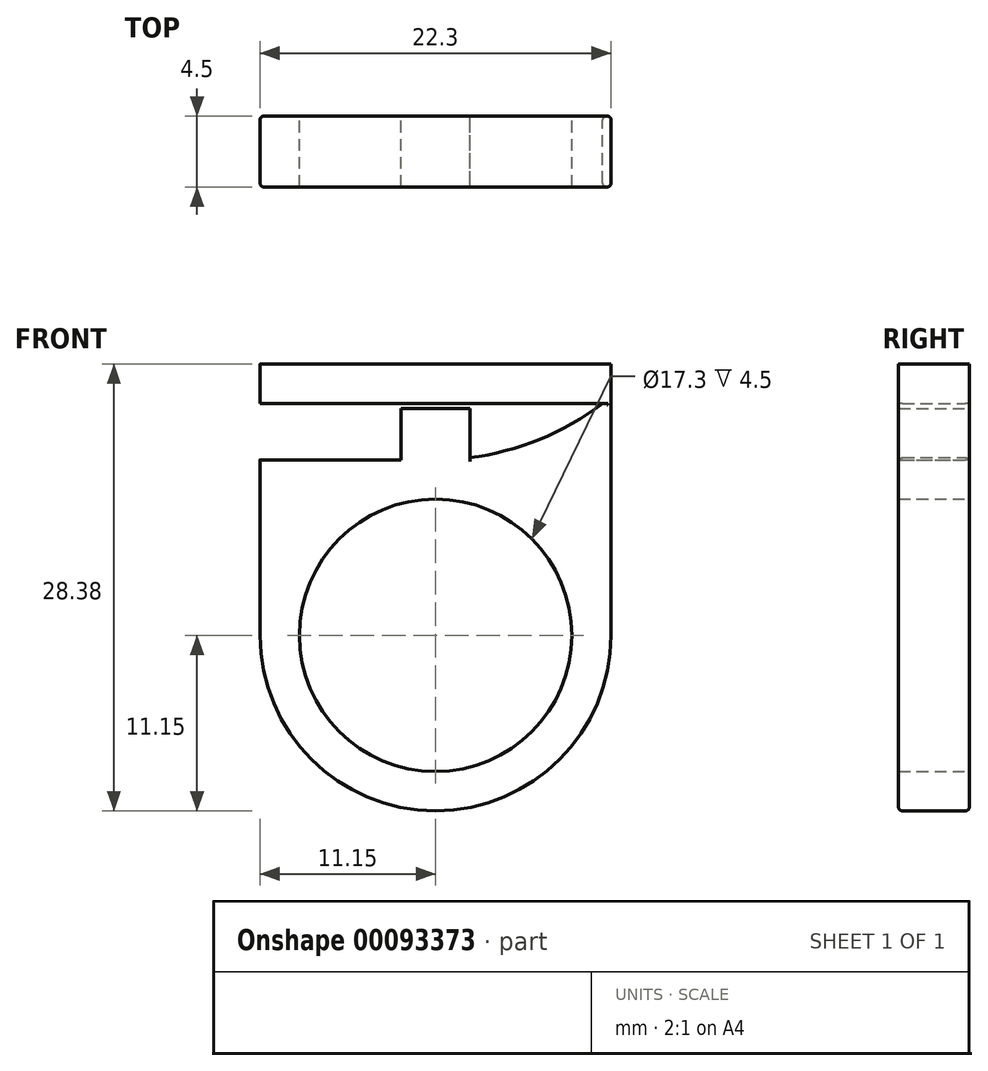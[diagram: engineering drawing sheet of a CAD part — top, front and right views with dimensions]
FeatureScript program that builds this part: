
annotation { "Feature Type Name" : "Feature", "Feature Type Description" : "" }
export const myFeature = defineFeature(function(context is Context, id is Id, definition is map)
    precondition{}
    {
        {
            var Q0;
            Q0=qCreatedBy(makeId("Front.planeOp"),FACE);
            var sketch = newSketch(context, id + "F0", { "sketchPlane" : qUnion([Q0])});
            skCircle(sketch, "E0", {"center": v(0, 0) * mm, "radius": 8.65 * mm});
            skCircle(sketch, "E1.0", {"center": v(0, 0) * mm, "radius": 11.15 * mm});
            skPoint(sketch, "E2", {"position": v(0, 11.15) * mm});
            skPoint(sketch, "E3", {"position": v(11.15, 0) * mm});
            skPoint(sketch, "E4", {"position": v(-11.15, 0) * mm});
            skLineSegment(sketch, "E5", {"start": v(11.15, 0) * mm, "end": v(11.15, 11.15) * mm});
            skLineSegment(sketch, "E6", {"start": v(11.15, 11.15) * mm, "end": v(0, 11.15) * mm});
            skLineSegment(sketch, "E7.MirrorCS", {"start": v(-11.15, 11.15) * mm, "end": v(0, 11.15) * mm});
            skLineSegment(sketch, "E8.MirrorCS", {"start": v(-11.15, 0) * mm, "end": v(-11.15, 11.15) * mm});
            skLineSegment(sketch, "E9", {"start": v(0, 11.15) * mm, "end": v(0, 13.15) * mm, "construction": true});
            skArc(sketch, "E10", {"start": v(0, 11.15) * mm, "mid": v(2, 13.15) * mm, "end": v(0, 15.15) * mm, "construction": true});
            skLineSegment(sketch, "E11", {"start": v(0, 15.15) * mm, "end": v(-11.15, 15.15) * mm});
            skLineSegment(sketch, "E12", {"start": v(-11.15, 15.15) * mm, "end": v(-11.15, 17.23) * mm});
            skLineSegment(sketch, "E13", {"start": v(-11.15, 17.23) * mm, "end": v(11.15, 17.23) * mm});
            skLineSegment(sketch, "E14", {"start": v(11.15, 17.23) * mm, "end": v(11.15, 15.15) * mm});
            skLineSegment(sketch, "E15", {"start": v(11.15, 15.15) * mm, "end": v(0, 15.15) * mm});
            skLineSegment(sketch, "E16", {"start": v(0, 13.15) * mm, "end": v(2, 13.15) * mm});
            skLineSegment(sketch, "E17.MirrorCS", {"start": v(0, 13.15) * mm, "end": v(-2, 13.15) * mm});
            skLineSegment(sketch, "E18", {"start": v(-11.15, 15.15) * mm, "end": v(-11.15, 11.15) * mm, "construction": true});
            skLineSegment(sketch, "E19", {"start": v(-11.15, 13.15) * mm, "end": v(-9.15, 13.15) * mm, "construction": true});
            skArc(sketch, "E20", {"start": v(-9.15, 15.15) * mm, "mid": v(-11.15, 13.15) * mm, "end": v(-9.15, 11.15) * mm, "construction": true});
            skPoint(sketch, "E21", {"position": v(-4, 15.15) * mm});
            skPoint(sketch, "E22", {"position": v(-4, 11.15) * mm});
            skPoint(sketch, "E23", {"position": v(-9.15, 15.15) * mm});
            skPoint(sketch, "E24", {"position": v(-9.15, 11.15) * mm});
            skLineSegment(sketch, "E25", {"start": v(0, 13.15) * mm, "end": v(-4, 13.15) * mm});
            skArc(sketch, "E26", {"start": v(-4, 15.15) * mm, "mid": v(-6, 13.15) * mm, "end": v(-4, 11.15) * mm, "construction": true});
            skArc(sketch, "E27", {"start": v(0, 11.15) * mm, "mid": v(5.92, 12.18) * mm, "end": v(11.15, 15.15) * mm});
            skLineSegment(sketch, "E28", {"start": v(11.15, 15.15) * mm, "end": v(11.15, 11.15) * mm});
            skArc(sketch, "E29.MirrorCS", {"start": v(0, 11.15) * mm, "mid": v(-5.92, 12.18) * mm, "end": v(-11.15, 15.15) * mm});
            skLineSegment(sketch, "E30", {"start": v(-11.15, 15.15) * mm, "end": v(-11.15, 11.15) * mm});
            skLineSegment(sketch, "E31", {"start": v(2.18, 10.75) * mm, "end": v(2.18, 14.42) * mm});
            skLineSegment(sketch, "E32", {"start": v(2.18, 14.42) * mm, "end": v(0, 14.42) * mm});
            skLineSegment(sketch, "E33.MirrorCS", {"start": v(-2.18, 14.42) * mm, "end": v(0, 14.42) * mm});
            skLineSegment(sketch, "E34.MirrorCS", {"start": v(-2.18, 10.75) * mm, "end": v(-2.18, 14.42) * mm});
            skPoint(sketch, "E35.start.orphan", {"position": v(0, 10.75) * mm});
            skPoint(sketch, "E36.MirrorCS.end.orphan", {"position": v(-2.18, 10.75) * mm});
            skLineSegment(sketch, "E37", {"start": v(-11.15, 14.71) * mm, "end": v(11.15, 14.71) * mm});
            skSolve(sketch);
        }
        {
            var Q0;
            Q0=makeQuery(id+"F0.imprint","IMPRINT",FACE,{"disambiguationData":[TD([[makeQuery(id+"F0.imprint","IMPRINT",EDGE,{"derivedFrom":sQuery(id+"F0.wireOp",EDGE,"E0")}),-1.0]])]});
            var Q1;
            {var subQ0=sQuery(id+"F0.wireOp",EDGE,"E7.MirrorCS");Q1=makeQuery(id+"F0.imprint","IMPRINT",FACE,{"disambiguationData":[TD([[makeQuery(id+"F0.imprint","IMPRINT",EDGE,{"derivedFrom":subQ0}),-1.0]])]});}
            var Q2;
            {var subQ0=sQuery(id+"F0.wireOp",EDGE,"E5");Q2=makeQuery(id+"F0.imprint","IMPRINT",FACE,{"disambiguationData":[TD([[makeQuery(id+"F0.imprint","IMPRINT",EDGE,{"derivedFrom":subQ0}),1.0]])]});}
            var Q3;
            Q3=makeQuery(id+"F0.imprint","IMPRINT",FACE,{"disambiguationData":[TD([[makeQuery(id+"F0.imprint","IMPRINT",EDGE,{"derivedFrom":sQuery(id+"F0.wireOp",EDGE,"E7.MirrorCS")}),1.0]])]});
            var Q4;
            {var subQ0=sQuery(id+"F0.wireOp",EDGE,"E30");Q4=makeQuery(id+"F0.imprint","IMPRINT",FACE,{"disambiguationData":[TD([[makeQuery(id+"F0.imprint","IMPRINT",EDGE,{"derivedFrom":subQ0}),1.0]])]});}
            var Q5;
            {var subQ0=sQuery(id+"F0.wireOp",EDGE,"E8.MirrorCS");Q5=makeQuery(id+"F0.imprint","IMPRINT",FACE,{"disambiguationData":[TD([[makeQuery(id+"F0.imprint","IMPRINT",EDGE,{"derivedFrom":subQ0}),-1.0]])]});}
            var Q6;
            {var subQ0=sQuery(id+"F0.wireOp",EDGE,"E28");Q6=makeQuery(id+"F0.imprint","IMPRINT",FACE,{"disambiguationData":[TD([[makeQuery(id+"F0.imprint","IMPRINT",EDGE,{"derivedFrom":subQ0}),-1.0]])]});}
            var Q7;
            {var subQ1=sQuery(id+"F0.wireOp",EDGE,"E1.0");var subQ3=sQuery(id+"F0.wireOp",EDGE,"E31");var subQ4=makeQuery(id+"F0.imprint","INTERSECT",VERTEX,{"derivedFrom":[subQ1,subQ3]});Q7=makeQuery(id+"F0.imprint","IMPRINT",FACE,{"disambiguationData":[TD([[makeQuery(id+"F0.imprint","IMPRINT",EDGE,{"disambiguationData":[TD([[subQ4,-1.0]])],"derivedFrom":subQ3}),1.0]])]});}
            var Q8;
            {var subQ1=sQuery(id+"F0.wireOp",EDGE,"E6");var subQ3=sQuery(id+"F0.wireOp",EDGE,"E31");var subQ4=makeQuery(id+"F0.imprint","INTERSECT",VERTEX,{"derivedFrom":[subQ1,subQ3]});Q8=makeQuery(id+"F0.imprint","IMPRINT",FACE,{"disambiguationData":[TD([[makeQuery(id+"F0.imprint","IMPRINT",EDGE,{"disambiguationData":[TD([[subQ4,-1.0]])],"derivedFrom":subQ3}),1.0]])]});}
            var Q9;
            {var subQ0=sQuery(id+"F0.wireOp",EDGE,"E31");var subQ3=sQuery(id+"F0.wireOp",EDGE,"E27");var subQ4=makeQuery(id+"F0.imprint","INTERSECT",VERTEX,{"derivedFrom":[subQ3,subQ0]});Q9=makeQuery(id+"F0.imprint","IMPRINT",FACE,{"disambiguationData":[TD([[makeQuery(id+"F0.imprint","IMPRINT",EDGE,{"disambiguationData":[TD([[subQ4,-1.0]])],"derivedFrom":subQ3}),-1.0]])]});}
            var Q10;
            {var subQ0=sQuery(id+"F0.wireOp",EDGE,"E34.MirrorCS");var subQ3=sQuery(id+"F0.wireOp",EDGE,"E29.MirrorCS");var subQ4=makeQuery(id+"F0.imprint","INTERSECT",VERTEX,{"derivedFrom":[subQ3,subQ0]});Q10=makeQuery(id+"F0.imprint","IMPRINT",FACE,{"disambiguationData":[TD([[makeQuery(id+"F0.imprint","IMPRINT",EDGE,{"disambiguationData":[TD([[subQ4,-1.0]])],"derivedFrom":subQ3}),1.0]])]});}
            var Q11;
            Q11=makeQuery(id+"F0.imprint","IMPRINT",FACE,{"disambiguationData":[TD([[makeQuery(id+"F0.imprint","IMPRINT",EDGE,{"derivedFrom":sQuery(id+"F0.wireOp",EDGE,"E11")}),-1.0]])]});
            var Q12;
            {var subQ1=sQuery(id+"F0.wireOp",EDGE,"E11");Q12=makeQuery(id+"F0.imprint","IMPRINT",FACE,{"disambiguationData":[TD([[makeQuery(id+"F0.imprint","IMPRINT",EDGE,{"derivedFrom":subQ1}),1.0]])]});}
            extrude(context, id + "F1", {"entities" : qUnion([Q0, Q1, Q2, Q3, Q4, Q5, Q6, Q7, Q8, Q9, Q10, Q11, Q12]), "depth" : 2.25 * mm, "hasSecondDirection" : true, "secondDirectionOppositeDirection" : true, "secondDirectionDepth" : 2.25 * mm});
        }
        {
            var Q0;
            Q0=makeQuery(id+"F1.opExtrude","CAP_EDGE",EDGE,{"disambiguationData":[OSD([sQuery(id+"F0.wireOp",EDGE,"E27"),sQuery(id+"F0.wireOp",EDGE,"E29.MirrorCS")])],"isStart":false});
            var Q1;
            Q1=makeQuery(id+"F1.opExtrude","CAP_EDGE",EDGE,{"disambiguationData":[OSD([sQuery(id+"F0.wireOp",EDGE,"E1.0")])],"isStart":false});
            var Q2;
            Q2=makeQuery(id+"F1.opExtrude","CAP_EDGE",EDGE,{"disambiguationData":[OSD([sQuery(id+"F0.wireOp",EDGE,"E27"),sQuery(id+"F0.wireOp",EDGE,"E29.MirrorCS")])],"isStart":true});
            var Q3;
            Q3=makeQuery(id+"F1.opExtrude","CAP_EDGE",EDGE,{"disambiguationData":[OSD([sQuery(id+"F0.wireOp",EDGE,"E1.0")])],"isStart":true});
            var Q4;
            Q4=makeQuery(id+"F1.opExtrude","CAP_EDGE",EDGE,{"disambiguationData":[OSD([sQuery(id+"F0.wireOp",EDGE,"E5"),sQuery(id+"F0.wireOp",EDGE,"E14"),sQuery(id+"F0.wireOp",EDGE,"E28")])],"isStart":false});
            var Q5;
            Q5=makeQuery(id+"F1.opExtrude","CAP_EDGE",EDGE,{"disambiguationData":[OSD([sQuery(id+"F0.wireOp",EDGE,"E5"),sQuery(id+"F0.wireOp",EDGE,"E14"),sQuery(id+"F0.wireOp",EDGE,"E28")])],"isStart":true});
            var Q6;
            Q6=makeQuery(id+"F1.opExtrude","CAP_EDGE",EDGE,{"disambiguationData":[OSD([sQuery(id+"F0.wireOp",EDGE,"E8.MirrorCS"),sQuery(id+"F0.wireOp",EDGE,"E12"),sQuery(id+"F0.wireOp",EDGE,"E30")])],"isStart":false});
            var Q7;
            Q7=makeQuery(id+"F1.opExtrude","CAP_EDGE",EDGE,{"disambiguationData":[OSD([sQuery(id+"F0.wireOp",EDGE,"E8.MirrorCS"),sQuery(id+"F0.wireOp",EDGE,"E12"),sQuery(id+"F0.wireOp",EDGE,"E30")])],"isStart":true});
            fillet(context, id + "F2", {"entities" : qUnion([Q0, Q1, Q2, Q3, Q4, Q5, Q6, Q7]), "radius" : .25 * mm, "tangentPropagation" : true, "allowEdgeOverflow" : false});
        }
    });
